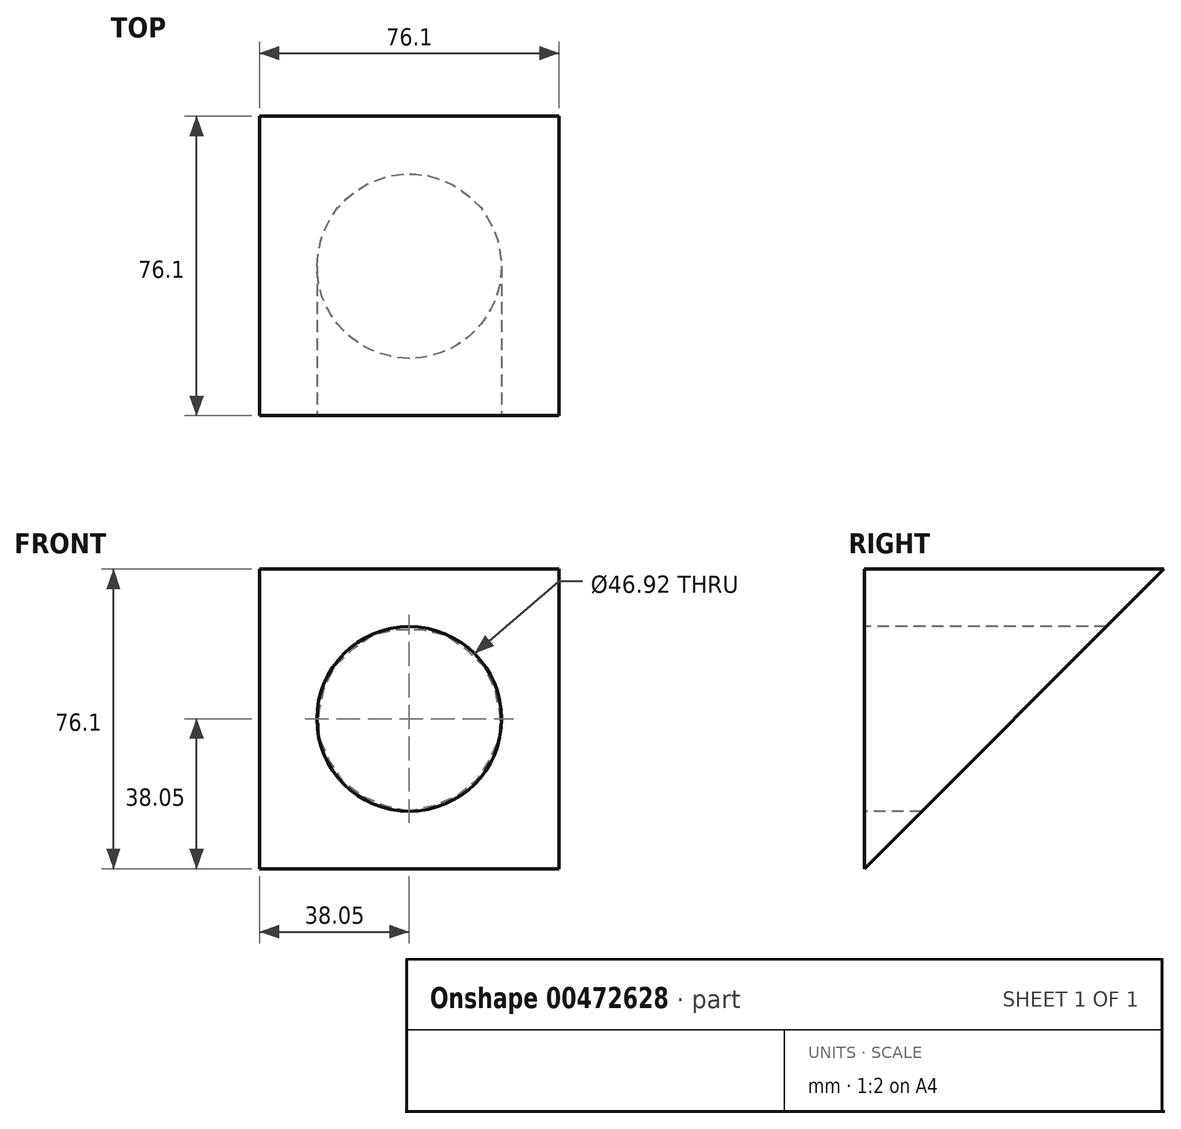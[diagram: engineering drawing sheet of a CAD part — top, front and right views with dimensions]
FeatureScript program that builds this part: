
annotation { "Feature Type Name" : "Feature", "Feature Type Description" : "" }
export const myFeature = defineFeature(function(context is Context, id is Id, definition is map)
    precondition{}
    {
        {
            var Q0;
            Q0=qCreatedBy(makeId("Front.planeOp"),FACE);
            var sketch = newSketch(context, id + "F0", { "sketchPlane" : qUnion([Q0])});
            skLineSegment(sketch, "E0.bottom", {"start": v(-38.05, 38.05) * mm, "end": v(38.05, 38.05) * mm});
            skLineSegment(sketch, "E0.top", {"start": v(-38.05, -38.05) * mm, "end": v(38.05, -38.05) * mm});
            skLineSegment(sketch, "E0.left", {"start": v(-38.05, 38.05) * mm, "end": v(-38.05, -38.05) * mm});
            skLineSegment(sketch, "E0.right", {"start": v(38.05, 38.05) * mm, "end": v(38.05, -38.05) * mm});
            skPoint(sketch, "E0.middle", {"position": v(0, 0) * mm});
            skSolve(sketch);
        }
        {
            var Q0;
            Q0 = qSketchRegion(id + "F0", true);
            extrude(context, id + "F1", {"entities" : qUnion([Q0]), "depth" : 76.1 * mm});
        }
        {
            var Q0;
            Q0=makeQuery(id+"F1.opExtrude","SWEPT_FACE",FACE,{"disambiguationData":[OSD([sQuery(id+"F0.wireOp",EDGE,"E0.left")])]});
            var sketch = newSketch(context, id + "F2", { "sketchPlane" : qUnion([Q0])});
            skLineSegment(sketch, "E1", {"start": v(0, 38.05) * mm, "end": v(76.1, -38.05) * mm});
            skLineSegment(sketch, "E2", {"start": v(76.1, -38.05) * mm, "end": v(0, -38.05) * mm});
            skLineSegment(sketch, "E3", {"start": v(0, -38.05) * mm, "end": v(0, 38.05) * mm});
            skSolve(sketch);
        }
        {
            var Q0;
            Q0 = qSketchRegion(id + "F2", true);
            extrude(context, id + "F3", {"entities" : qUnion([Q0]), "operationType" : NewBodyOperationType.REMOVE, "oppositeDirection" : true, "depth" : 76.1 * mm});
        }
        {
            var Q0;
            Q0=makeQuery(id+"F1.opExtrude","CAP_FACE",FACE,{"disambiguationData":[OSD([sQuery(id+"F0.wireOp",EDGE,"E0.bottom"),sQuery(id+"F0.wireOp",EDGE,"E0.top"),sQuery(id+"F0.wireOp",EDGE,"E0.left"),sQuery(id+"F0.wireOp",EDGE,"E0.right")])],"isStart":false});
            var sketch = newSketch(context, id + "F4", { "sketchPlane" : qUnion([Q0])});
            skCircle(sketch, "E4", {"center": v(0, 0) * mm, "radius": 23.46 * mm});
            skSolve(sketch);
        }
        {
            var Q0;
            Q0 = qSketchRegion(id + "F4", true);
            extrude(context, id + "F5", {"entities" : qUnion([Q0]), "operationType" : NewBodyOperationType.REMOVE, "oppositeDirection" : true, "depth" : 63.5 * mm});
        }
    });
